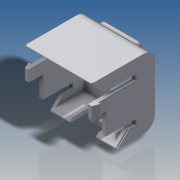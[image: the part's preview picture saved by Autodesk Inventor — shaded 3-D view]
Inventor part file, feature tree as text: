
AUTODESK INVENTOR PART (.ipt)
format: ipt  version: 2016 SP2 (Build 200236200, 236)  size: 558,080 bytes
history: native  units: in
note: dims shown in document units (in); Inventor stores cm internally (conversion verified against a paired STEP export)
features: extrude x9, sketch x5, mirror x1, fillet x1, projected_geometry x1
ambient origin geometry x8: Origin, YZ Plane, XZ Plane, XY Plane, X Axis, Y Axis, Z Axis, Center Point
bodies: Solid1 (feature_tree)
feature tree (17):
  sketch  "Sketch2"  dims[d0=0.8504in d1=0.1417in]
  extrude  "Extrusion1"  Depth=0.1417in
  extrude  "Extrusion2"  Depth=0.2362in
  extrude  "Extrusion3"  Depth=0.7717in
  extrude  "Extrusion4"  Depth=0.1417in
  extrude  "Extrusion5"  Depth=0.3937in
  extrude  "Extrusion6"  Depth=0.3937in
  mirror  "Mirror1"
  extrude  "Extrusion7"  Depth=0.3937in
  extrude  "Extrusion8"  Depth=0.3937in
  extrude  "Extrusion9"  Depth=0.3937in
  fillet  "Fillet1"  Radius=0.8189in
  sketch  "Sketch3"  dims[d2=0.4724in d3=0.2362in]
  sketch  "Sketch4"  dims[d4=0.5984in d5=0.7717in]
  projected_geometry  "Projected Loop1"
  sketch  "Sketch5"  dims[d6=45.0deg d7=0.1417in]
  sketch  "Sketch7"  dims[d8=0.4094in d9=0.0157in d10=0.1417in d11=0.0567in d12=0.0472in d13=0.0945in d14=0.8189in d15=0.0in d16=0.7244in d17=0.0in d18=0.0472in d19=0.0472in d20=0.063in d21=0.0472in d22=0.0472in d23=0.063in d24=0.0315in d25=0.315in d26=0.0in d27=0.189in d28=0.0in d29=0.063in d30=0.0in d31=0.0157in d32=0.0157in d33=0.0079in d34=0.0in d35=0.0787in d36=0.0315in d37=0.0079in d38=0.0in d39=0.5732in d40=0.4724in d41=0.0378in d42=0.0079in d43=0.0in d44=0.0039in d45=0.1732in d46=0.063in d47=0.0189in d48=0.3937in d49=0.0in]
